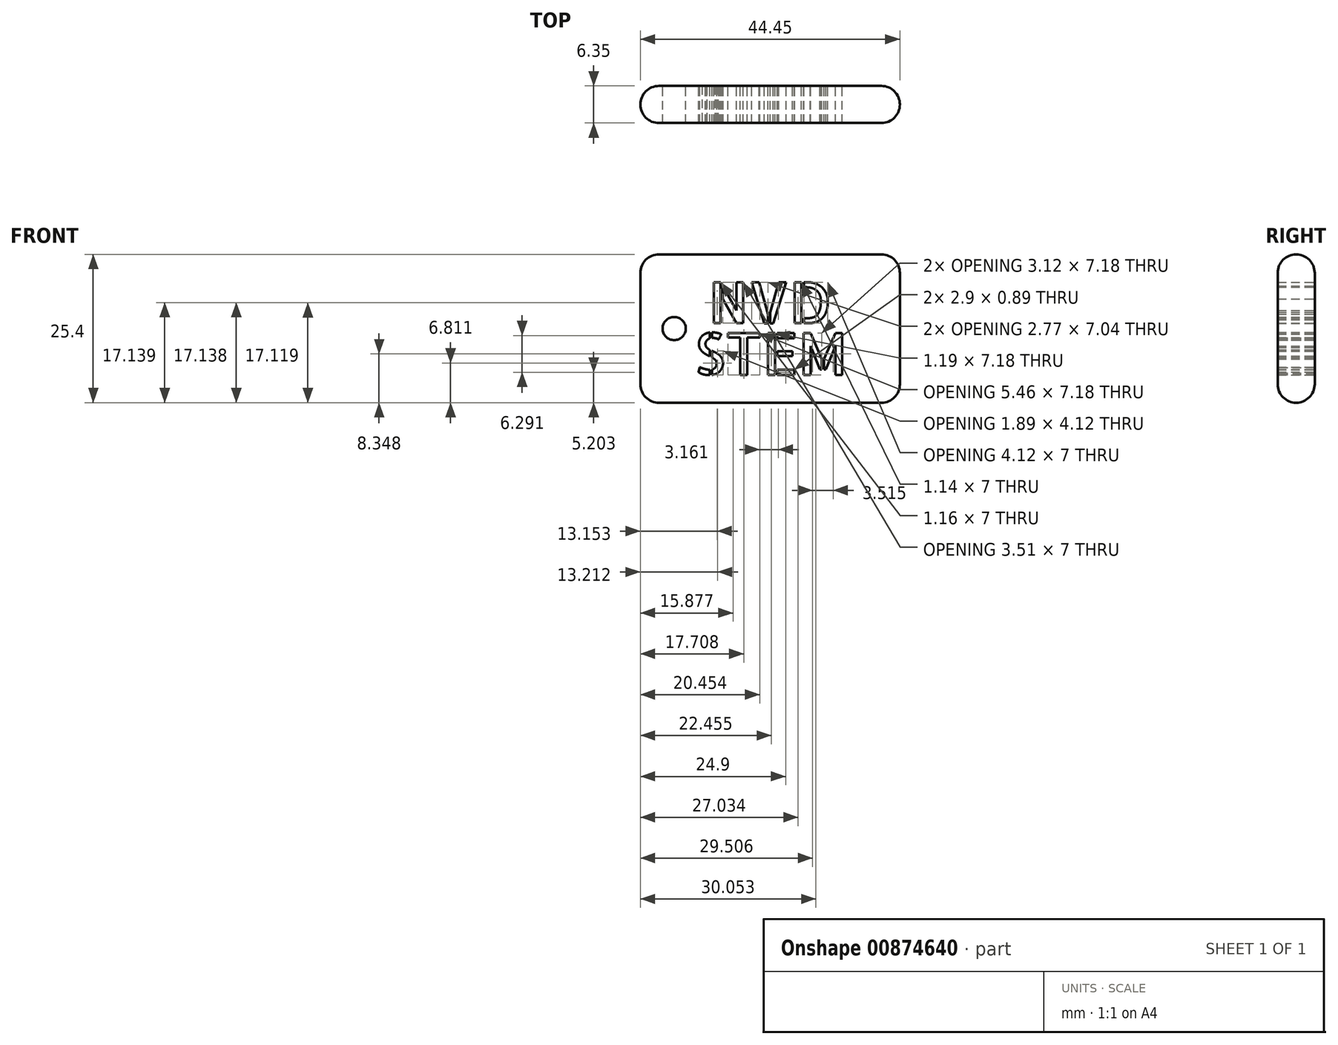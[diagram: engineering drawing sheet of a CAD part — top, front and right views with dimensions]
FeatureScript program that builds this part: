
annotation { "Feature Type Name" : "Feature", "Feature Type Description" : "" }
export const myFeature = defineFeature(function(context is Context, id is Id, definition is map)
    precondition{}
    {
        {
            var Q0;
            Q0=qCreatedBy(makeId("Front.planeOp"),FACE);
            var sketch = newSketch(context, id + "F0", { "sketchPlane" : qUnion([Q0])});
            skLineSegment(sketch, "E0.bottom", {"start": v(0, 0) * mm, "end": v(44.45, 0) * mm});
            skLineSegment(sketch, "E0.top", {"start": v(0, 25.4) * mm, "end": v(44.45, 25.4) * mm});
            skLineSegment(sketch, "E0.left", {"start": v(0, 0) * mm, "end": v(0, 25.4) * mm});
            skLineSegment(sketch, "E0.right", {"start": v(44.45, 0) * mm, "end": v(44.45, 25.4) * mm});
            skText(sketch, "E1", { "text": "NVD", "fontName": "AllertaStencil-Regular.ttf"});
            skText(sketch, "E2", { "text": "STEM", "fontName": "AllertaStencil-Regular.ttf"});
            skLineSegment(sketch, "E3", {"start": v(22.23, 13.64) * mm, "end": v(22.23, 11.95) * mm, "construction": true});
            skLineSegment(sketch, "E4", {"start": v(22.23, 20.64) * mm, "end": v(22.23, 25.4) * mm, "construction": true});
            skCircle(sketch, "E5", {"center": v(5.8, 12.7) * mm, "radius": 1.98 * mm});
            skPoint(sketch, "E6.visualSharp", {"position": v(44.45, 25.4) * mm});
            skLineSegment(sketch, "E6.filletArc", {"start": v(44.45, 25.4) * mm, "end": v(44.45, 25.4) * mm});
            skPoint(sketch, "E7.visualSharp", {"position": v(44.45, 0) * mm});
            skLineSegment(sketch, "E7.filletArc", {"start": v(44.45, 0) * mm, "end": v(44.45, 0) * mm});
            skPoint(sketch, "E8.visualSharp", {"position": v(0, 0) * mm});
            skLineSegment(sketch, "E8.filletArc", {"start": v(0, 0) * mm, "end": v(0, 0) * mm});
            skPoint(sketch, "E9.visualSharp", {"position": v(0, 25.4) * mm});
            skLineSegment(sketch, "E9.filletArc", {"start": v(0, 25.4) * mm, "end": v(0, 25.4) * mm});
            const initialGuessF0  = {"E1": [0.0117, 0.01364, 1, 0, 0.007], "E2": [0.0092, 0.00476, 1, 0, 0.00718]};
            skSetInitialGuess(sketch, initialGuessF0);
            skSolve(sketch);
        }
        {
            var Q0;
            Q0=makeQuery(id+"F0.imprint","IMPRINT",FACE,{"disambiguationData":[TD([[makeQuery(id+"F0.imprint","IMPRINT",EDGE,{"derivedFrom":sQuery(id+"F0.wireOp",EDGE,"E0.bottom")}),1.0]])]});
            extrude(context, id + "F1", {"entities" : qUnion([Q0]), "depth" : 6.35 * mm, "offsetDistance" : 25.4 * mm});
        }
        {
            var Q0;
            Q0=makeQuery(id+"F1.opExtrude","CAP_EDGE",EDGE,{"disambiguationData":[OSD([sQuery(id+"F0.wireOp",EDGE,"E0.top")])],"isStart":false});
            var Q1;
            Q1=makeQuery(id+"F1.opExtrude","CAP_EDGE",EDGE,{"disambiguationData":[OSD([sQuery(id+"F0.wireOp",EDGE,"E0.bottom")])],"isStart":false});
            var Q2;
            Q2=makeQuery(id+"F1.opExtrude","CAP_EDGE",EDGE,{"disambiguationData":[OSD([sQuery(id+"F0.wireOp",EDGE,"E0.right")])],"isStart":false});
            var Q3;
            Q3=makeQuery(id+"F1.opExtrude","CAP_EDGE",EDGE,{"disambiguationData":[OSD([sQuery(id+"F0.wireOp",EDGE,"E0.left")])],"isStart":false});
            var Q4;
            Q4=makeQuery(id+"F1.opExtrude","CAP_EDGE",EDGE,{"disambiguationData":[OSD([sQuery(id+"F0.wireOp",EDGE,"E0.top")])],"isStart":true});
            var Q5;
            Q5=makeQuery(id+"F1.opExtrude","CAP_EDGE",EDGE,{"disambiguationData":[OSD([sQuery(id+"F0.wireOp",EDGE,"E0.right")])],"isStart":true});
            var Q6;
            Q6=makeQuery(id+"F1.opExtrude","CAP_EDGE",EDGE,{"disambiguationData":[OSD([sQuery(id+"F0.wireOp",EDGE,"E0.left")])],"isStart":true});
            var Q7;
            Q7=makeQuery(id+"F1.opExtrude","CAP_EDGE",EDGE,{"disambiguationData":[OSD([sQuery(id+"F0.wireOp",EDGE,"E0.bottom")])],"isStart":true});
            fillet(context, id + "F2", {"entities" : qUnion([Q0, Q1, Q2, Q3, Q4, Q5, Q6, Q7]), "radius" : 3.17 * mm, "tangentPropagation" : true, "allowEdgeOverflow" : false});
        }
        {
            var Q0;
            Q0=makeQuery(id+"F2.opFillet","BLEND_EDGE",EDGE,{"blendedFrom":[makeQuery(id+"F1.opExtrude","CAP_EDGE",EDGE,{"disambiguationData":[OSD([sQuery(id+"F0.wireOp",EDGE,"E0.bottom")])],"isStart":true}),makeQuery(id+"F1.opExtrude","CAP_EDGE",EDGE,{"disambiguationData":[OSD([sQuery(id+"F0.wireOp",EDGE,"E0.left")])],"isStart":true})],"blendedInto":[]});
            var Q1;
            Q1=makeQuery(id+"F2.opFillet","BLEND_EDGE",EDGE,{"blendedFrom":[makeQuery(id+"F1.opExtrude","CAP_EDGE",EDGE,{"disambiguationData":[OSD([sQuery(id+"F0.wireOp",EDGE,"E0.bottom")])],"isStart":true}),makeQuery(id+"F1.opExtrude","CAP_EDGE",EDGE,{"disambiguationData":[OSD([sQuery(id+"F0.wireOp",EDGE,"E0.right")])],"isStart":true})],"blendedInto":[]});
            var Q2;
            Q2=makeQuery(id+"F2.opFillet","BLEND_EDGE",EDGE,{"blendedFrom":[makeQuery(id+"F1.opExtrude","CAP_EDGE",EDGE,{"disambiguationData":[OSD([sQuery(id+"F0.wireOp",EDGE,"E0.top")])],"isStart":true}),makeQuery(id+"F1.opExtrude","CAP_EDGE",EDGE,{"disambiguationData":[OSD([sQuery(id+"F0.wireOp",EDGE,"E0.right")])],"isStart":true})],"blendedInto":[]});
            var Q3;
            Q3=makeQuery(id+"F2.opFillet","BLEND_EDGE",EDGE,{"blendedFrom":[makeQuery(id+"F1.opExtrude","CAP_EDGE",EDGE,{"disambiguationData":[OSD([sQuery(id+"F0.wireOp",EDGE,"E0.top")])],"isStart":true}),makeQuery(id+"F1.opExtrude","CAP_EDGE",EDGE,{"disambiguationData":[OSD([sQuery(id+"F0.wireOp",EDGE,"E0.left")])],"isStart":true})],"blendedInto":[]});
            fillet(context, id + "F3", {"entities" : qUnion([Q0, Q1, Q2, Q3]), "radius" : 3.17 * mm, "tangentPropagation" : true, "allowEdgeOverflow" : false});
        }
    });
